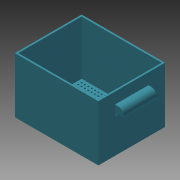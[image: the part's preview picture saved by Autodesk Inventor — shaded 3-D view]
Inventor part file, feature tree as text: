
AUTODESK INVENTOR PART (.ipt)
format: ipt  version: 2015 (Build 190159000, 159)  size: 446,464 bytes
history: native  units: mm
features: extrude x4, sketch x4, pattern_linear x3, fillet x2, shell x1
ambient origin geometry x8: Origin, YZ Plane, XZ Plane, XY Plane, X Axis, Y Axis, Z Axis, Center Point
bodies: 实体1 (feature_tree)
feature tree (14):
  extrude  "拉伸1"  Depth=120.0mm
  shell  "抽壳1"  Thickness=100.0mm
  extrude  "拉伸2"  Depth=3.0mm
  pattern_linear  "矩形阵列1"  Count1=10 Spacing1=0.0mm
  pattern_linear  "矩形阵列2"  Count1=18 Spacing1=6.0mm
  extrude  "拉伸3"  Depth=10.0mm
  extrude  "拉伸4"  Depth=60.0mm
  pattern_linear  "矩形阵列3"  Count1=2  [1 undecoded]
  fillet  "圆角1"  Radius=30.0mm
  fillet  "圆角2"  Radius=20.0mm
  sketch  "草图1"  dims[d0=150.0mm d1=120.0mm d2=100.0mm d3=0.0mm]
  sketch  "草图2"  dims[d4=3.0mm d5=3.0mm]
  sketch  "草图3"  dims[d6=6.0mm]
  sketch  "草图4"  dims[d7=6.0mm d8=100.0mm d9=0.0mm d10=180.0mm d12=6.0mm d13=230.0mm d15=6.0mm d16=60.0mm d17=20.0mm d18=30.0mm d19=20.0mm d20=15.0mm d21=0.0mm d22=15.0mm d23=60.0mm d24=0.0mm d25=20.0mm d27=165.0mm d28=2.0mm d29=10.0mm]
note: 1 required parameter value undecoded (feature->parameter linkage not recoverable at this tier; creation-order binding heuristic only, values carry confidence <= 0.55)
